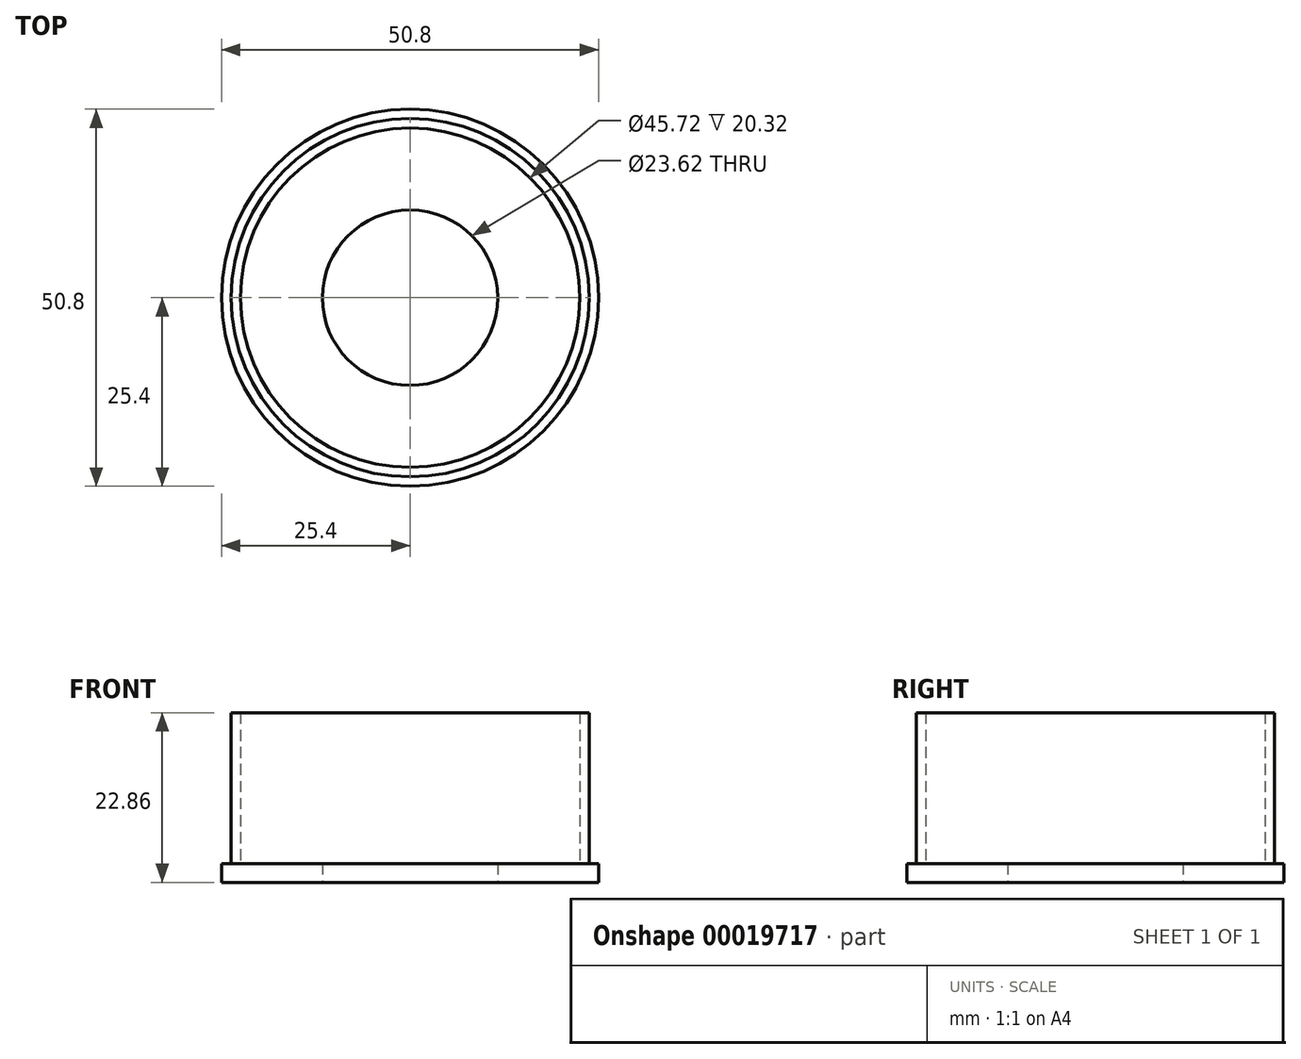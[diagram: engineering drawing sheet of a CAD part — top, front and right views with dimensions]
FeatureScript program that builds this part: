
annotation { "Feature Type Name" : "Feature", "Feature Type Description" : "" }
export const myFeature = defineFeature(function(context is Context, id is Id, definition is map)
    precondition{}
    {
        {
            var Q0;
            Q0=qCreatedBy(makeId("Top.planeOp"),FACE);
            var sketch = newSketch(context, id + "F0", { "sketchPlane" : qUnion([Q0])});
            skCircle(sketch, "E0", {"center": v(0, 0) * mm, "radius": 22.86 * mm});
            skCircle(sketch, "E1", {"center": v(0, 0) * mm, "radius": 24.13 * mm});
            skSolve(sketch);
        }
        {
            var Q0;
            Q0=makeQuery(id+"F0.imprint","IMPRINT",FACE,{"disambiguationData":[TD([[makeQuery(id+"F0.imprint","IMPRINT",EDGE,{"derivedFrom":sQuery(id+"F0.wireOp",EDGE,"E0")}),-1.0]])]});
            var Q1;
            Q1=sQuery(id+"F0.wireOp",EDGE,"E1");
            var Q2;
            Q2=sQuery(id+"F0.wireOp",EDGE,"E0");
            extrude(context, id + "F1", {"entities" : qUnion([Q0]), "surfaceEntities" : qUnion([Q1, Q2]), "depth" : 22.86 * mm});
        }
        {
            var Q0;
            Q0=qCreatedBy(makeId("Top.planeOp"),FACE);
            var sketch = newSketch(context, id + "F2", { "sketchPlane" : qUnion([Q0])});
            skCircle(sketch, "E2", {"center": v(0, 0) * mm, "radius": 25.4 * mm});
            skCircle(sketch, "E3", {"center": v(0, 0) * mm, "radius": 11.81 * mm});
            skCircle(sketch, "E4", {"center": v(0, 0) * mm, "radius": 13.92 * mm});
            skSolve(sketch);
        }
        {
            var Q0;
            Q0=makeQuery(id+"F2.imprint","IMPRINT",FACE,{"disambiguationData":[TD([[makeQuery(id+"F2.imprint","IMPRINT",EDGE,{"derivedFrom":sQuery(id+"F2.wireOp",EDGE,"E3")}),-1.0]])]});
            var Q1;
            Q1=makeQuery(id+"F2.imprint","IMPRINT",FACE,{"disambiguationData":[TD([[makeQuery(id+"F2.imprint","IMPRINT",EDGE,{"derivedFrom":sQuery(id+"F2.wireOp",EDGE,"E2")}),1.0]])]});
            extrude(context, id + "F3", {"entities" : qUnion([Q0, Q1]), "operationType" : NewBodyOperationType.ADD, "depth" : 2.54 * mm});
        }
    });
